FCSTD DOCUMENT  (FreeCAD 0.21R33771 (Git))
Label: sensor_placement
License: All rights reserved
LicenseURL: https://en.wikipedia.org/wiki/All_rights_reserved
objects: Part::Part2DObjectPython×17, App::MeasureDistance×3
note: 17 computed .brp shape members not serialized (recipe doc carries the construction recipe); baked Part::Feature solids carry a one-line shape summary decoded from their .brp

FEATURE [Part::Part2DObjectPython] Line  label="camper_high"  # Draft 2D object (typed FeaturePython)
  Area = 0
  ChamferSize = 0
  Closed = true
  End = (0,3000,0)
  FilletRadius = 0
  Length = 3000
  MakeFace = true
  Points = (2) [(0,0,0),(0,3000,0)]
  Start = (0,0,0)
  Subdivisions = 0
FEATURE [Part::Part2DObjectPython] Line001  label="ground_line"  # Draft 2D object (typed FeaturePython)
  Area = 0
  ChamferSize = 0
  Closed = false
  End = (2000,0,0)
  FilletRadius = 0
  Length = 2000
  MakeFace = true
  Points = (2) [(0,0,0),(2000,0,0)]
  Start = (0,0,0)
  Subdivisions = 0
FEATURE [Part::Part2DObjectPython] Circle006  # Draft 2D object (typed FeaturePython)
  Area = 1.9635e+07
  FirstAngle = 0
  LastAngle = 0
  MakeFace = true
  Placement = pos=(15595.3,4260.43,0) rot=(0,0,1;0rad)
  Radius = 2500
FEATURE [Part::Part2DObjectPython] Line012  # Draft 2D object (typed FeaturePython)
  Area = 0
  ChamferSize = 0
  Closed = false
  End = (11084.6,5400.29,0)
  FilletRadius = 0
  Length = 2200
  MakeFace = true
  Placement = pos=(11084.6,3200.29,0) rot=(0,0,1;0rad)
  Points = (2) [(0,0,0),(0,2200,0)]
  Start = (11084.6,3200.29,0)
  Subdivisions = 0
FEATURE [Part::Part2DObjectPython] Line013  # Draft 2D object (typed FeaturePython)
  Area = 0
  ChamferSize = 0
  Closed = false
  End = (16710.6,5400.29,0)
  FilletRadius = 0
  Length = 5626
  MakeFace = true
  Placement = pos=(11084.6,5400.29,0) rot=(0,0,1;0rad)
  Points = (2) [(0,0,0),(5626,0,0)]
  Start = (11084.6,5400.29,0)
  Subdivisions = 0
FEATURE [Part::Part2DObjectPython] Line014  # Draft 2D object (typed FeaturePython)
  Area = 0
  ChamferSize = 0
  Closed = false
  End = (16710.6,3200.29,0)
  FilletRadius = 0
  Length = 6040.85
  MakeFace = true
  Placement = pos=(11084.6,5400.29,0) rot=(0,0,1;0rad)
  Points = (2) [(0,0,0),(5626,-2200,0)]
  Start = (11084.6,5400.29,0)
  Subdivisions = 0
FEATURE [Part::Part2DObjectPython] Line015  # Draft 2D object (typed FeaturePython)
  Area = 0
  ChamferSize = 0
  Closed = false
  End = (11084.6,3200.29,0)
  FilletRadius = 0
  Length = 6040.85
  MakeFace = true
  Placement = pos=(16710.6,5400.29,0) rot=(0,0,1;0rad)
  Points = (2) [(0,0,0),(-5626,-2200,0)]
  Start = (16710.6,5400.29,0)
  Subdivisions = 0
FEATURE [Part::Part2DObjectPython] Line016  # Draft 2D object (typed FeaturePython)
  Area = 0
  ChamferSize = 0
  Closed = false
  End = (16710.6,3200.29,0)
  FilletRadius = 0
  Length = 5626
  MakeFace = true
  Placement = pos=(11084.6,3200.29,0) rot=(0,0,1;0rad)
  Points = (2) [(0,0,0),(5626,0,0)]
  Start = (11084.6,3200.29,0)
  Subdivisions = 0
FEATURE [Part::Part2DObjectPython] Line017  # Draft 2D object (typed FeaturePython)
  Area = 0
  ChamferSize = 0
  Closed = false
  End = (16710.6,5400.29,0)
  FilletRadius = 0
  Length = 2200
  MakeFace = true
  Placement = pos=(16710.6,3200.29,0) rot=(0,0,1;0rad)
  Points = (2) [(0,0,0),(0,2200,0)]
  Start = (16710.6,3200.29,0)
  Subdivisions = 0
FEATURE [Part::Part2DObjectPython] Circle007  # Draft 2D object (typed FeaturePython)
  Area = 1.9635e+07
  FirstAngle = 0
  LastAngle = 0
  MakeFace = true
  Placement = pos=(8015.7,4391.43,0) rot=(0,0,1;0rad)
  Radius = 2500
FEATURE [Part::Part2DObjectPython] Line019  # Draft 2D object (typed FeaturePython)
  Area = 0
  ChamferSize = 0
  Closed = false
  End = (39425.6,-6006.71,0)
  FilletRadius = 0
  Length = 2200
  MakeFace = true
  Placement = pos=(39425.6,-8206.71,0) rot=(0,0,1;0rad)
  Points = (2) [(0,0,0),(0,2200,0)]
  Start = (39425.6,-8206.71,0)
  Subdivisions = 0
FEATURE [Part::Part2DObjectPython] Line020  # Draft 2D object (typed FeaturePython)
  Area = 0
  ChamferSize = 0
  Closed = false
  End = (33799.6,-6006.71,0)
  FilletRadius = 0
  Length = 2200
  MakeFace = true
  Placement = pos=(33799.6,-8206.71,0) rot=(0,0,1;0rad)
  Points = (2) [(0,0,0),(0,2200,0)]
  Start = (33799.6,-8206.71,0)
  Subdivisions = 0
FEATURE [Part::Part2DObjectPython] Line021  # Draft 2D object (typed FeaturePython)
  Area = 0
  ChamferSize = 0
  Closed = false
  End = (39425.6,-6006.71,0)
  FilletRadius = 0
  Length = 5626
  MakeFace = true
  Placement = pos=(33799.6,-6006.71,0) rot=(0,0,1;0rad)
  Points = (2) [(0,0,0),(5626,0,0)]
  Start = (33799.6,-6006.71,0)
  Subdivisions = 0
FEATURE [Part::Part2DObjectPython] Line022  # Draft 2D object (typed FeaturePython)
  Area = 0
  ChamferSize = 0
  Closed = false
  End = (39425.6,-8206.71,0)
  FilletRadius = 0
  Length = 6040.85
  MakeFace = true
  Placement = pos=(33799.6,-6006.71,0) rot=(0,0,1;0rad)
  Points = (2) [(0,0,0),(5626,-2200,0)]
  Start = (33799.6,-6006.71,0)
  Subdivisions = 0
FEATURE [Part::Part2DObjectPython] Line023  # Draft 2D object (typed FeaturePython)
  Area = 0
  ChamferSize = 0
  Closed = false
  End = (33799.6,-8206.71,0)
  FilletRadius = 0
  Length = 6040.85
  MakeFace = true
  Placement = pos=(39425.6,-6006.71,0) rot=(0,0,1;0rad)
  Points = (2) [(0,0,0),(-5626,-2200,0)]
  Start = (39425.6,-6006.71,0)
  Subdivisions = 0
FEATURE [Part::Part2DObjectPython] Line024  # Draft 2D object (typed FeaturePython)
  Area = 0
  ChamferSize = 0
  Closed = false
  End = (39425.6,-8206.71,0)
  FilletRadius = 0
  Length = 5626
  MakeFace = true
  Placement = pos=(33799.6,-8206.71,0) rot=(0,0,1;0rad)
  Points = (2) [(0,0,0),(5626,0,0)]
  Start = (33799.6,-8206.71,0)
  Subdivisions = 0
FEATURE [Part::Part2DObjectPython] Circle  # Draft 2D object (typed FeaturePython)
  Area = 4.11657e+07
  FirstAngle = 0
  LastAngle = 0
  MakeFace = true
  Placement = pos=(36575.5,-7092.19,0) rot=(0,0,1;0rad)
  Radius = 3619.87
FEATURE [App::MeasureDistance] Distance004  label="Distance: 2515,95 mm"
  Distance = 2515.95
  P1 = (36615,-5991.14,2.274e-13)
  P2 = (36603.3,-3475.21,0)
FEATURE [App::MeasureDistance] Distance005  label="Distance: 569,58 mm"
  Distance = 569.581
  P1 = (39425.6,-6006.71,0)
  P2 = (39929.8,-5741.78,0)
FEATURE [App::MeasureDistance] Distance006  label="Distance: 7234,98 mm"
  Distance = 7234.98
  P1 = (32960.4,-7116.96,0)
  P2 = (40195.4,-7092.19,0)
